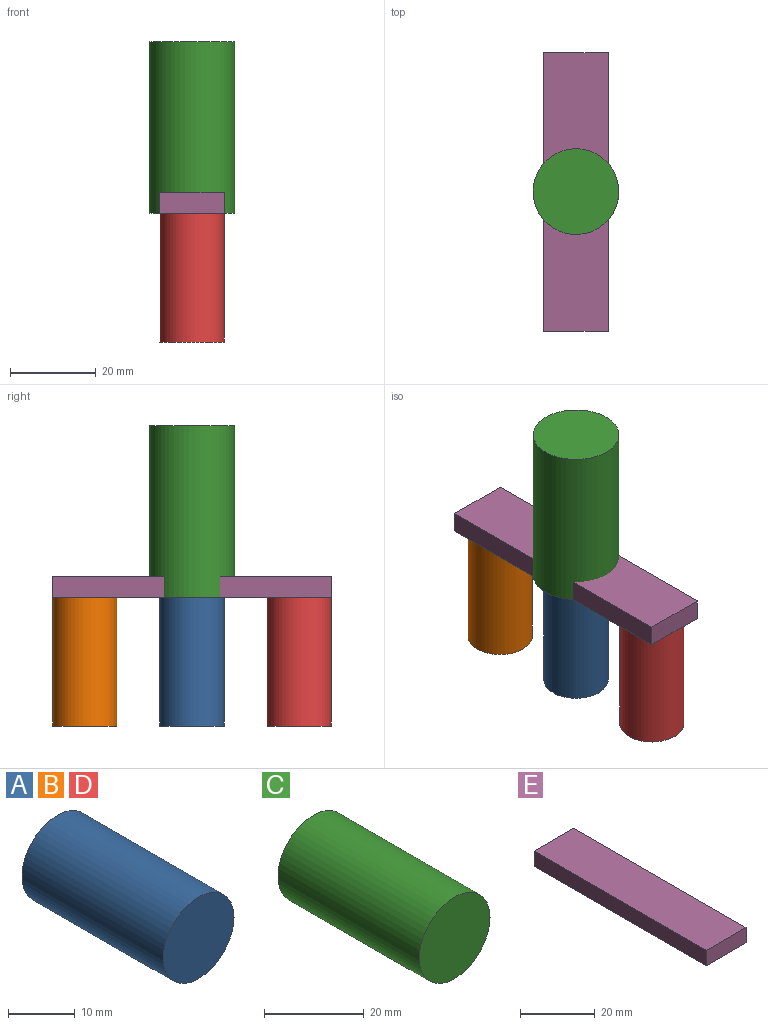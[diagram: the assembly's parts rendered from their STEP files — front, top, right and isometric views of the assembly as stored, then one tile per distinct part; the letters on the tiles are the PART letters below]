
ASSEMBLY  parts=5 mates=4
PART A: 3 faces, bbox 15x30x15 mm
  f0: cylinder r=7.5mm len=30mm, axis (0,1,0), area 1413.7mm2, adj f1,f2
  f1: plane 15x15mm, normal (0,-1,0), area 176.7mm2, adj f0
  f2: plane 15x15mm, normal (0,1,0), area 176.7mm2, adj f0
PART B: same geometry as A
PART C: 3 faces, bbox 20x40x20 mm
  f0: cylinder r=10mm len=40mm, axis (0,1,0), area 2513.3mm2, adj f1,f2
  f1: plane 20x20mm, normal (0,-1,0), area 314.2mm2, adj f0
  f2: plane 20x20mm, normal (0,1,0), area 314.2mm2, adj f0
PART D: same geometry as A
PART E: 6 faces, bbox 15x65x5 mm
  f0: plane 65x15mm, normal (0,0,-1), area 975mm2, adj f1,f3,f4,f5
  f1: plane 65x5mm, normal (1,0,0), area 325mm2, adj f0,f2,f4,f5
  f2: plane 65x15mm, normal (0,0,1), area 975mm2, adj f1,f3,f4,f5
  f3: plane 65x5mm, normal (-1,0,0), area 325mm2, adj f0,f2,f4,f5
  f4: plane 15x5mm, normal (0,-1,0), area 75mm2, adj f0,f1,f2,f3
  f5: plane 15x5mm, normal (0,1,0), area 75mm2, adj f0,f1,f2,f3
PLACE A rot(axis=(1,0,0),90deg) t=(-25.23,17.78,-3.77)mm
PLACE B rot(axis=(1,0,0),90deg) t=(-25.23,42.78,-3.77)mm
PLACE C rot(axis=(1,0,0),90deg) t=(-25.23,17.78,36.23)mm
PLACE D rot(axis=(1,0,0),90deg) t=(-25.23,-7.22,-3.77)mm
PLACE E t=(-25.23,50.28,-1.27)mm
MATE fastened D.f0 <-> E.f0  axis (0,0,1) through (-25.23,-7.22,-3.77)mm
MATE fastened C.f0 <-> E.f0  axis (0,0,-1) through (-25.23,17.78,-3.77)mm
MATE fastened A.f0 <-> E.f0  axis (0,0,1) through (-25.23,17.78,-3.77)mm
MATE fastened B.f0 <-> E.f0  axis (0,0,1) through (-25.23,42.78,-3.77)mm
